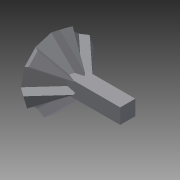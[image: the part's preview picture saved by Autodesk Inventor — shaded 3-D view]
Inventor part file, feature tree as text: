
AUTODESK INVENTOR PART (.ipt)
format: ipt  version: 2015 (Build 190159000, 159)  size: 134,656 bytes
history: native  units: in
note: dims shown in document units (in); Inventor stores cm internally (conversion verified against a paired STEP export)
features: extrude x4, sketch x4, pattern_circular x1
ambient origin geometry x8: Origin, YZ Plane, XZ Plane, XY Plane, X Axis, Y Axis, Z Axis, Center Point
bodies: Body1 (feature_tree)
feature tree (9):
  extrude  "Extrusion2"  Depth=0.24in
  extrude  "Extrusion3"  Depth=0.05in
  extrude  "Extrusion4"  Depth=0.1in
  extrude  "Extrusion5"  Depth=0.001in TaperAngle=0.0deg
  pattern_circular  "Circular Pattern1"  Count=6 Angle=360.0deg
  sketch  "Sketch6"  dims[d27=0.2in d28=0.24in d29=-0.3092in]
  sketch  "Sketch7"  dims[d30=0.29in d31=0.05in d32=-0.0687in]
  sketch  "Sketch8"  dims[d33=0.1in d34=0.1in]
  sketch  "Sketch9"  dims[d35=0.5in d36=0.0in d37=0.001in d38=0.0in d39=2.3622in d40=360.0deg]
